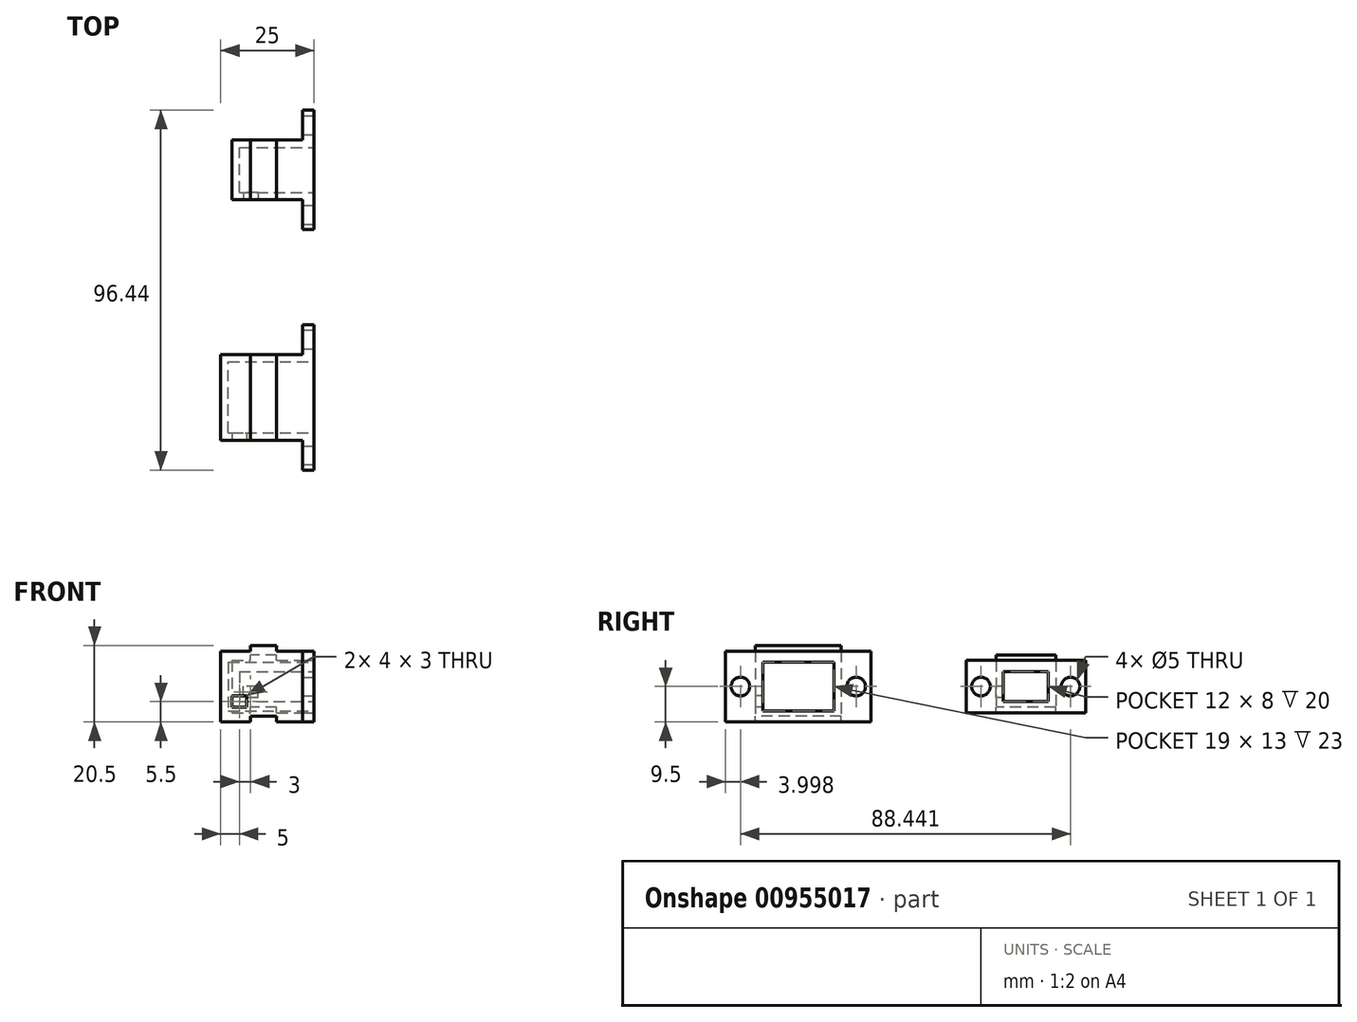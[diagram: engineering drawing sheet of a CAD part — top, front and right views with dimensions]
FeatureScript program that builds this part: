
annotation { "Feature Type Name" : "Feature", "Feature Type Description" : "" }
export const myFeature = defineFeature(function(context is Context, id is Id, definition is map)
    precondition{}
    {
        {
            var Q0;
            Q0=qCreatedBy(makeId("Right.planeOp"),FACE);
            var sketch = newSketch(context, id + "F0", { "sketchPlane" : qUnion([Q0])});
            skLineSegment(sketch, "E0.bottom", {"start": v(-59.66, 9.5) * mm, "end": v(-36.66, 9.5) * mm});
            skLineSegment(sketch, "E0.top", {"start": v(-59.66, -9.5) * mm, "end": v(-36.66, -9.5) * mm});
            skLineSegment(sketch, "E0.left", {"start": v(-59.66, 9.5) * mm, "end": v(-59.66, -9.5) * mm});
            skLineSegment(sketch, "E0.right", {"start": v(-36.66, 9.5) * mm, "end": v(-36.66, -9.5) * mm});
            skPoint(sketch, "E0.middle", {"position": v(-48.16, 0) * mm});
            skLineSegment(sketch, "E1.0", {"start": v(-57.66, 6.5) * mm, "end": v(-38.66, 6.5) * mm});
            skLineSegment(sketch, "E1.1", {"start": v(-57.66, 6.5) * mm, "end": v(-57.66, -6.5) * mm});
            skLineSegment(sketch, "E1.2", {"start": v(-57.66, -6.5) * mm, "end": v(-38.66, -6.5) * mm});
            skLineSegment(sketch, "E1.3", {"start": v(-38.66, 6.5) * mm, "end": v(-38.66, -6.5) * mm});
            skLineSegment(sketch, "E2.bottom", {"start": v(-59.66, 9.5) * mm, "end": v(-67.66, 9.5) * mm});
            skLineSegment(sketch, "E2.top", {"start": v(-59.66, -9.5) * mm, "end": v(-67.66, -9.5) * mm});
            skLineSegment(sketch, "E2.right", {"start": v(-67.66, 9.5) * mm, "end": v(-67.66, -9.5) * mm});
            skLineSegment(sketch, "E3.bottom", {"start": v(-36.66, 9.5) * mm, "end": v(-28.66, 9.5) * mm});
            skLineSegment(sketch, "E3.top", {"start": v(-36.66, -9.5) * mm, "end": v(-28.66, -9.5) * mm});
            skLineSegment(sketch, "E3.right", {"start": v(-28.66, 9.5) * mm, "end": v(-28.66, -9.5) * mm});
            skCircle(sketch, "E4", {"center": v(-63.66, 0) * mm, "radius": 2.5 * mm});
            skLineSegment(sketch, "E5", {"start": v(-67.66, 0) * mm, "end": v(-63.66, 0) * mm, "construction": true});
            skLineSegment(sketch, "E6", {"start": v(-63.66, 0) * mm, "end": v(-59.66, 0) * mm, "construction": true});
            skCircle(sketch, "E7", {"center": v(-32.66, 0) * mm, "radius": 2.5 * mm});
            skLineSegment(sketch, "E8", {"start": v(-36.66, 0) * mm, "end": v(-32.66, 0) * mm, "construction": true});
            skLineSegment(sketch, "E9", {"start": v(-32.66, 0) * mm, "end": v(-28.66, 0) * mm, "construction": true});
            skLineSegment(sketch, "E10.bottom", {"start": v(4.78, 7) * mm, "end": v(20.78, 7) * mm});
            skLineSegment(sketch, "E10.top", {"start": v(4.78, -7) * mm, "end": v(20.78, -7) * mm});
            skLineSegment(sketch, "E10.left", {"start": v(4.78, 7) * mm, "end": v(4.78, -7) * mm});
            skLineSegment(sketch, "E10.right", {"start": v(20.78, 7) * mm, "end": v(20.78, -7) * mm});
            skPoint(sketch, "E10.middle", {"position": v(12.78, 0) * mm});
            skLineSegment(sketch, "E11.0", {"start": v(6.78, 4) * mm, "end": v(18.78, 4) * mm});
            skLineSegment(sketch, "E11.1", {"start": v(6.78, 4) * mm, "end": v(6.78, -4) * mm});
            skLineSegment(sketch, "E11.2", {"start": v(6.78, -4) * mm, "end": v(18.78, -4) * mm});
            skLineSegment(sketch, "E11.3", {"start": v(18.78, 4) * mm, "end": v(18.78, -4) * mm});
            skLineSegment(sketch, "E12.bottom", {"start": v(4.78, 7) * mm, "end": v(-3.22, 7) * mm});
            skLineSegment(sketch, "E12.top", {"start": v(4.78, -7) * mm, "end": v(-3.22, -7) * mm});
            skLineSegment(sketch, "E12.right", {"start": v(-3.22, 7) * mm, "end": v(-3.22, -7) * mm});
            skLineSegment(sketch, "E13.bottom", {"start": v(20.78, 7) * mm, "end": v(28.78, 7) * mm});
            skLineSegment(sketch, "E13.top", {"start": v(20.78, -7) * mm, "end": v(28.78, -7) * mm});
            skLineSegment(sketch, "E13.right", {"start": v(28.78, 7) * mm, "end": v(28.78, -7) * mm});
            skCircle(sketch, "E14", {"center": v(0.78, 0) * mm, "radius": 2.5 * mm});
            skLineSegment(sketch, "E15", {"start": v(-3.22, 0) * mm, "end": v(0.78, 0) * mm, "construction": true});
            skLineSegment(sketch, "E16", {"start": v(0.78, 0) * mm, "end": v(4.78, 0) * mm, "construction": true});
            skCircle(sketch, "E17", {"center": v(24.78, 0) * mm, "radius": 2.5 * mm});
            skLineSegment(sketch, "E18", {"start": v(20.78, 0) * mm, "end": v(24.78, 0) * mm, "construction": true});
            skLineSegment(sketch, "E19", {"start": v(24.78, 0) * mm, "end": v(28.78, 0) * mm, "construction": true});
            skLineSegment(sketch, "E20", {"start": v(4.78, 1.54) * mm, "end": v(6.78, 1.54) * mm, "construction": true});
            skLineSegment(sketch, "E21", {"start": v(18.78, 1.63) * mm, "end": v(20.78, 1.63) * mm, "construction": true});
            skSolve(sketch);
        }
        {
            var Q0;
            {var subQ3=sQuery(id+"F0.wireOp",EDGE,"E0.bottom");Q0=makeQuery(id+"F0.imprint","IMPRINT",FACE,{"disambiguationData":[TD([[makeQuery(id+"F0.imprint","IMPRINT",EDGE,{"derivedFrom":subQ3}),-1.0]])]});}
            extrude(context, id + "F1", {"entities" : qUnion([Q0]), "oppositeDirection" : true, "depth" : 23 * mm, "offsetDistance" : 25.4 * mm});
        }
        {
            var Q0;
            Q0=makeQuery(id+"F0.imprint","IMPRINT",FACE,{"disambiguationData":[TD([[makeQuery(id+"F0.imprint","IMPRINT",EDGE,{"derivedFrom":sQuery(id+"F0.wireOp",EDGE,"E2.bottom")}),1.0]])]});
            var Q1;
            Q1=makeQuery(id+"F0.imprint","IMPRINT",FACE,{"disambiguationData":[TD([[makeQuery(id+"F0.imprint","IMPRINT",EDGE,{"derivedFrom":sQuery(id+"F0.wireOp",EDGE,"E3.bottom")}),-1.0]])]});
            extrude(context, id + "F2", {"entities" : qUnion([Q0, Q1]), "operationType" : NewBodyOperationType.ADD, "oppositeDirection" : true, "depth" : 3 * mm, "offsetDistance" : 25.4 * mm});
        }
        {
            var Q0;
            Q0=makeQuery(id+"F1.opExtrude","CAP_FACE",FACE,{"disambiguationData":[OSD([sQuery(id+"F0.wireOp",EDGE,"E0.bottom"),sQuery(id+"F0.wireOp",EDGE,"E0.top"),sQuery(id+"F0.wireOp",EDGE,"E1.0"),sQuery(id+"F0.wireOp",EDGE,"E1.1"),sQuery(id+"F0.wireOp",EDGE,"E1.2"),sQuery(id+"F0.wireOp",EDGE,"E1.3"),sQuery(id+"F0.wireOp",EDGE,"E0.left"),sQuery(id+"F0.wireOp",EDGE,"E0.right")])],"isStart":false});
            var sketch = newSketch(context, id + "F3", { "sketchPlane" : qUnion([Q0])});
            skLineSegment(sketch, "E22.bottom", {"start": v(36.66, 9.5) * mm, "end": v(59.66, 9.5) * mm});
            skLineSegment(sketch, "E22.top", {"start": v(36.66, -9.5) * mm, "end": v(59.66, -9.5) * mm});
            skLineSegment(sketch, "E22.left", {"start": v(36.66, 9.5) * mm, "end": v(36.66, -9.5) * mm});
            skLineSegment(sketch, "E22.right", {"start": v(59.66, 9.5) * mm, "end": v(59.66, -9.5) * mm});
            skSolve(sketch);
        }
        {
            var Q0;
            Q0 = qSketchRegion(id + "F3", true);
            extrude(context, id + "F4", {"entities" : qUnion([Q0]), "operationType" : NewBodyOperationType.ADD, "depth" : 2 * mm, "offsetDistance" : 25.4 * mm});
        }
        {
            var Q0;
            Q0=makeQuery(id+"F4.boolean.opBoolean","MERGE",FACE,{"derivedFrom":[makeQuery(id+"F1.opExtrude","SWEPT_FACE",FACE,{"disambiguationData":[OSD([sQuery(id+"F0.wireOp",EDGE,"E0.left")])]}),makeQuery(id+"F4.opExtrude","SWEPT_FACE",FACE,{"disambiguationData":[OSD([sQuery(id+"F3.wireOp",EDGE,"E22.right")])]})]});
            var sketch = newSketch(context, id + "F5", { "sketchPlane" : qUnion([Q0])});
            skLineSegment(sketch, "E23.bottom", {"start": v(-22, -2.5) * mm, "end": v(-18, -2.5) * mm});
            skLineSegment(sketch, "E23.top", {"start": v(-22, -5.5) * mm, "end": v(-18, -5.5) * mm});
            skLineSegment(sketch, "E23.left", {"start": v(-22, -2.5) * mm, "end": v(-22, -5.5) * mm});
            skLineSegment(sketch, "E23.right", {"start": v(-18, -2.5) * mm, "end": v(-18, -5.5) * mm});
            skLineSegment(sketch, "E24.bottom", {"start": v(-10, -9.5) * mm, "end": v(-17, -9.5) * mm});
            skLineSegment(sketch, "E24.top", {"start": v(-10, -8) * mm, "end": v(-17, -8) * mm});
            skLineSegment(sketch, "E24.left", {"start": v(-17, -9.5) * mm, "end": v(-17, -8) * mm});
            skLineSegment(sketch, "E24.right", {"start": v(-10, -9.5) * mm, "end": v(-10, -8) * mm});
            skLineSegment(sketch, "E25.bottom", {"start": v(-10, 9.5) * mm, "end": v(-17, 9.5) * mm});
            skLineSegment(sketch, "E25.top", {"start": v(-10, 11) * mm, "end": v(-17, 11) * mm});
            skLineSegment(sketch, "E25.left", {"start": v(-10, 9.5) * mm, "end": v(-10, 11) * mm});
            skLineSegment(sketch, "E25.right", {"start": v(-17, 9.5) * mm, "end": v(-17, 11) * mm});
            skSolve(sketch);
        }
        {
            var Q0;
            Q0=makeQuery(id+"F5.imprint","IMPRINT",FACE,{"disambiguationData":[TD([[makeQuery(id+"F5.imprint","IMPRINT",EDGE,{"derivedFrom":sQuery(id+"F5.wireOp",EDGE,"E23.bottom")}),-1.0]])]});
            extrude(context, id + "F6", {"entities" : qUnion([Q0]), "operationType" : NewBodyOperationType.REMOVE, "oppositeDirection" : true, "depth" : 3 * mm, "offsetDistance" : 25.4 * mm});
        }
        {
            var Q0;
            Q0=makeQuery(id+"F5.imprint","IMPRINT",FACE,{"disambiguationData":[TD([[makeQuery(id+"F5.imprint","IMPRINT",EDGE,{"derivedFrom":sQuery(id+"F5.wireOp",EDGE,"E25.bottom")}),1.0]])]});
            extrude(context, id + "F7", {"entities" : qUnion([Q0]), "operationType" : NewBodyOperationType.ADD, "oppositeDirection" : true, "depth" : 23 * mm, "offsetDistance" : 25.4 * mm});
        }
        {
            var Q0;
            Q0=makeQuery(id+"F5.imprint","IMPRINT",FACE,{"disambiguationData":[TD([[makeQuery(id+"F5.imprint","IMPRINT",EDGE,{"derivedFrom":sQuery(id+"F5.wireOp",EDGE,"E24.bottom")}),1.0]])]});
            extrude(context, id + "F8", {"entities" : qUnion([Q0]), "operationType" : NewBodyOperationType.REMOVE, "oppositeDirection" : true, "depth" : 23 * mm, "offsetDistance" : 25.4 * mm});
        }
        {
            var Q0;
            Q0=makeQuery(id+"F0.imprint","IMPRINT",FACE,{"disambiguationData":[TD([[makeQuery(id+"F0.imprint","IMPRINT",EDGE,{"derivedFrom":sQuery(id+"F0.wireOp",EDGE,"E10.bottom")}),-1.0]])]});
            extrude(context, id + "F9", {"entities" : qUnion([Q0]), "oppositeDirection" : true, "depth" : 20 * mm, "offsetDistance" : 25.4 * mm});
        }
        {
            var Q0;
            Q0=makeQuery(id+"F0.imprint","IMPRINT",FACE,{"disambiguationData":[TD([[makeQuery(id+"F0.imprint","IMPRINT",EDGE,{"derivedFrom":sQuery(id+"F0.wireOp",EDGE,"E12.bottom")}),1.0]])]});
            var Q1;
            Q1=makeQuery(id+"F0.imprint","IMPRINT",FACE,{"disambiguationData":[TD([[makeQuery(id+"F0.imprint","IMPRINT",EDGE,{"derivedFrom":sQuery(id+"F0.wireOp",EDGE,"E13.bottom")}),-1.0]])]});
            extrude(context, id + "F10", {"entities" : qUnion([Q0, Q1]), "operationType" : NewBodyOperationType.ADD, "oppositeDirection" : true, "depth" : 3 * mm, "offsetDistance" : 25.4 * mm});
        }
        {
            var Q0;
            Q0=makeQuery(id+"F9.opExtrude","CAP_FACE",FACE,{"disambiguationData":[OSD([sQuery(id+"F0.wireOp",EDGE,"E10.bottom"),sQuery(id+"F0.wireOp",EDGE,"E10.top"),sQuery(id+"F0.wireOp",EDGE,"E11.0"),sQuery(id+"F0.wireOp",EDGE,"E11.1"),sQuery(id+"F0.wireOp",EDGE,"E11.2"),sQuery(id+"F0.wireOp",EDGE,"E11.3"),sQuery(id+"F0.wireOp",EDGE,"E10.left"),sQuery(id+"F0.wireOp",EDGE,"E10.right")])],"isStart":false});
            var sketch = newSketch(context, id + "F11", { "sketchPlane" : qUnion([Q0])});
            skLineSegment(sketch, "E26.bottom", {"start": v(-20.78, 7) * mm, "end": v(-4.78, 7) * mm});
            skLineSegment(sketch, "E26.top", {"start": v(-20.78, -7) * mm, "end": v(-4.78, -7) * mm});
            skLineSegment(sketch, "E26.left", {"start": v(-20.78, 7) * mm, "end": v(-20.78, -7) * mm});
            skLineSegment(sketch, "E26.right", {"start": v(-4.78, 7) * mm, "end": v(-4.78, -7) * mm});
            skSolve(sketch);
        }
        {
            var Q0;
            Q0 = qSketchRegion(id + "F11", true);
            extrude(context, id + "F12", {"entities" : qUnion([Q0]), "operationType" : NewBodyOperationType.ADD, "depth" : 2 * mm, "offsetDistance" : 25.4 * mm});
        }
        {
            var Q0;
            Q0=makeQuery(id+"F12.boolean.opBoolean","MERGE",FACE,{"derivedFrom":[makeQuery(id+"F9.opExtrude","SWEPT_FACE",FACE,{"disambiguationData":[OSD([sQuery(id+"F0.wireOp",EDGE,"E10.left")])]}),makeQuery(id+"F12.opExtrude","SWEPT_FACE",FACE,{"disambiguationData":[OSD([sQuery(id+"F11.wireOp",EDGE,"E26.right")])]})]});
            var sketch = newSketch(context, id + "F13", { "sketchPlane" : qUnion([Q0])});
            skLineSegment(sketch, "E27.bottom", {"start": v(-15, -3) * mm, "end": v(-19, -3) * mm});
            skLineSegment(sketch, "E27.top", {"start": v(-15, 0) * mm, "end": v(-19, 0) * mm});
            skLineSegment(sketch, "E27.left", {"start": v(-15, -3) * mm, "end": v(-15, 0) * mm});
            skLineSegment(sketch, "E27.right", {"start": v(-19, -3) * mm, "end": v(-19, 0) * mm});
            skLineSegment(sketch, "E28.bottom", {"start": v(-10, -7) * mm, "end": v(-17, -7) * mm});
            skLineSegment(sketch, "E28.top", {"start": v(-10, -5.5) * mm, "end": v(-17, -5.5) * mm});
            skLineSegment(sketch, "E28.left", {"start": v(-10, -7) * mm, "end": v(-10, -5.5) * mm});
            skLineSegment(sketch, "E28.right", {"start": v(-17, -7) * mm, "end": v(-17, -5.5) * mm});
            skLineSegment(sketch, "E29.bottom", {"start": v(-10, 7) * mm, "end": v(-17, 7) * mm});
            skLineSegment(sketch, "E29.top", {"start": v(-10, 8.5) * mm, "end": v(-17, 8.5) * mm});
            skLineSegment(sketch, "E29.left", {"start": v(-10, 7) * mm, "end": v(-10, 8.5) * mm});
            skLineSegment(sketch, "E29.right", {"start": v(-17, 7) * mm, "end": v(-17, 8.5) * mm});
            skSolve(sketch);
        }
        {
            var Q0;
            Q0=makeQuery(id+"F13.imprint","IMPRINT",FACE,{"disambiguationData":[TD([[makeQuery(id+"F13.imprint","IMPRINT",EDGE,{"derivedFrom":sQuery(id+"F13.wireOp",EDGE,"E27.bottom")}),-1.0]])]});
            extrude(context, id + "F14", {"entities" : qUnion([Q0]), "operationType" : NewBodyOperationType.REMOVE, "oppositeDirection" : true, "depth" : 3 * mm, "offsetDistance" : 25.4 * mm});
        }
        {
            var Q0;
            Q0=makeQuery(id+"F13.imprint","IMPRINT",FACE,{"disambiguationData":[TD([[makeQuery(id+"F13.imprint","IMPRINT",EDGE,{"derivedFrom":sQuery(id+"F13.wireOp",EDGE,"E28.bottom")}),1.0]])]});
            extrude(context, id + "F15", {"entities" : qUnion([Q0]), "operationType" : NewBodyOperationType.REMOVE, "oppositeDirection" : true, "depth" : 16 * mm, "offsetDistance" : 25.4 * mm});
        }
        {
            var Q0;
            Q0=makeQuery(id+"F13.imprint","IMPRINT",FACE,{"disambiguationData":[TD([[makeQuery(id+"F13.imprint","IMPRINT",EDGE,{"derivedFrom":sQuery(id+"F13.wireOp",EDGE,"E29.bottom")}),1.0]])]});
            extrude(context, id + "F16", {"entities" : qUnion([Q0]), "operationType" : NewBodyOperationType.ADD, "oppositeDirection" : true, "depth" : 16 * mm, "offsetDistance" : 25.4 * mm});
        }
    });
